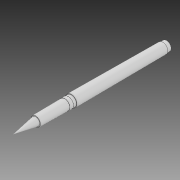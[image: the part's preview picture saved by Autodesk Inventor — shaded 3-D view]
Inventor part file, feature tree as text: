
AUTODESK INVENTOR PART (.ipt)
format: ipt  version: 2020 (Build 240168000, 168)  size: 110,080 bytes
history: native  units: mm
features: revolve x1, sketch x1
ambient origin geometry x8: Origin, YZ Plane, XZ Plane, XY Plane, X Axis, Y Axis, Z Axis, Center Point
bodies: Solid1 (feature_tree)
feature tree (2):
  revolve  "Revolution1"  [1 undecoded]
  sketch  "Sketch1"  dims[d0=3.875mm d1=3.2mm d2=4.25mm d3=4.8mm d4=80.3mm d5=4.325mm d6=2.5mm d7=3.0mm d8=4.4mm d9=4.25mm d10=4.0mm d11=3.375mm d12=129.1mm d13=30.0mm d14=90.0deg]
note: 1 required parameter value undecoded (feature->parameter linkage not recoverable at this tier; creation-order binding heuristic only, values carry confidence <= 0.55)
